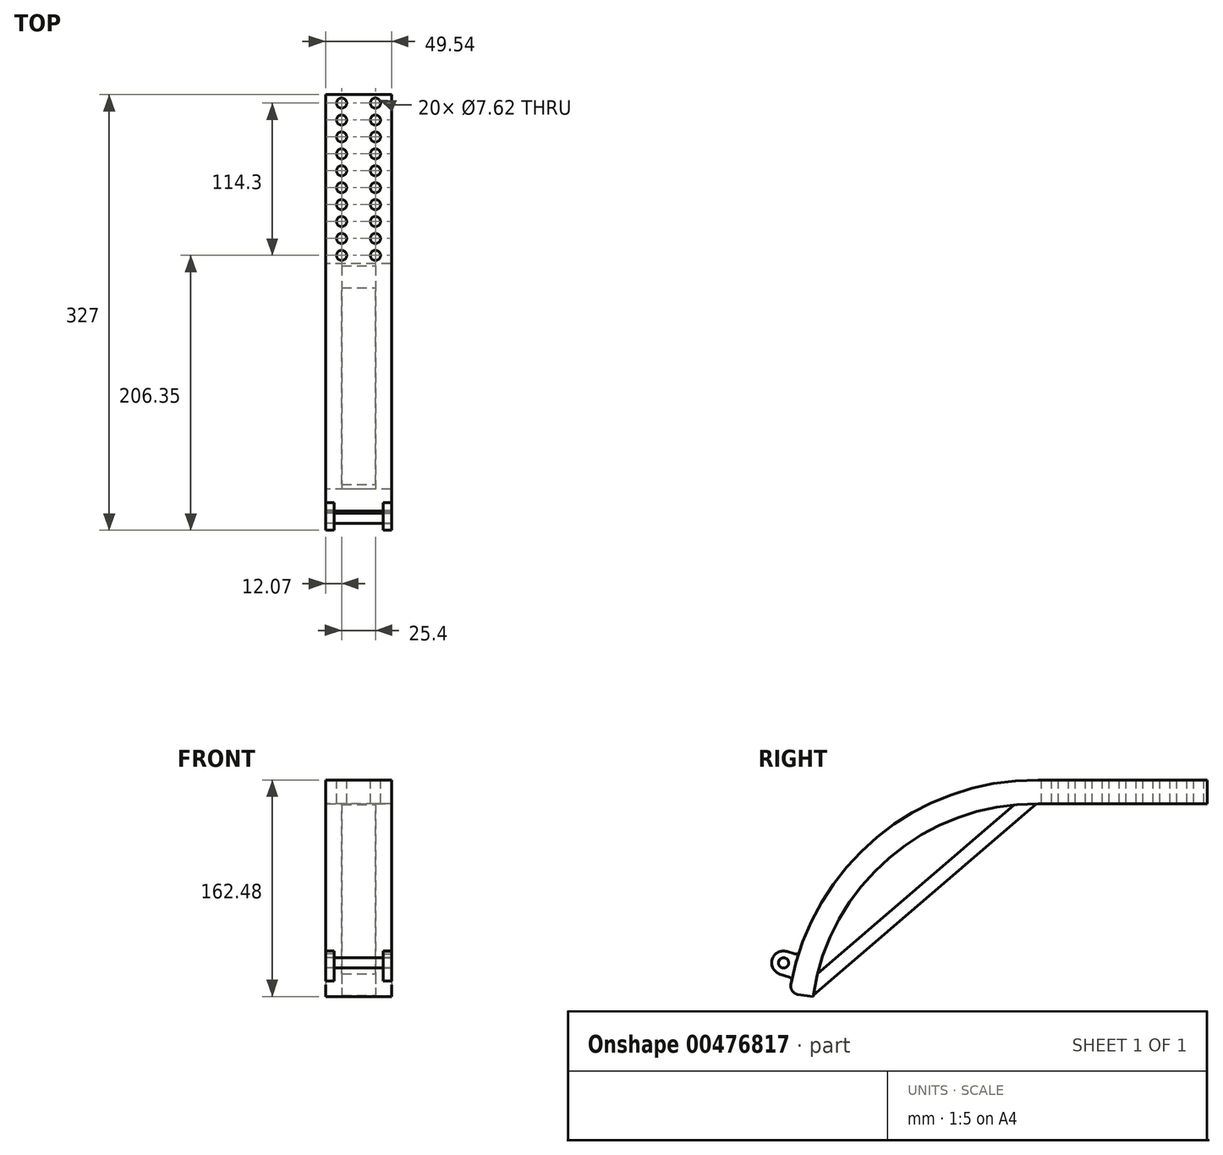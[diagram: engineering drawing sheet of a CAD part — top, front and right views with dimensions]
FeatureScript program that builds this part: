
annotation { "Feature Type Name" : "Feature", "Feature Type Description" : "" }
export const myFeature = defineFeature(function(context is Context, id is Id, definition is map)
    precondition{}
    {
        {
            var Q0;
            Q0=qCreatedBy(makeId("Front.planeOp"),FACE);
            var sketch = newSketch(context, id + "F0", { "sketchPlane" : qUnion([Q0])});
            skLineSegment(sketch, "E0.bottom", {"start": v(24.77, 8.9) * mm, "end": v(-24.77, 8.9) * mm});
            skLineSegment(sketch, "E0.top", {"start": v(24.77, -8.9) * mm, "end": v(-24.77, -8.9) * mm});
            skLineSegment(sketch, "E0.left", {"start": v(24.77, 8.9) * mm, "end": v(24.77, -8.9) * mm});
            skLineSegment(sketch, "E0.right", {"start": v(-24.77, 8.9) * mm, "end": v(-24.77, -8.9) * mm});
            skPoint(sketch, "E0.middle", {"position": v(0, 0) * mm});
            skSolve(sketch);
        }
        {
            var Q0;
            Q0=qCreatedBy(makeId("Right.planeOp"),FACE);
            var sketch = newSketch(context, id + "F1", { "sketchPlane" : qUnion([Q0])});
            skArc(sketch, "E1", {"start": v(0, 0) * mm, "mid": v(-117.53, -42.8) * mm, "end": v(-177.8, -152.4) * mm});
            skSolve(sketch);
        }
        {
            var Q0;
            Q0=makeQuery(id+"F0.imprint","IMPRINT",FACE,{"disambiguationData":[TD([[makeQuery(id+"F0.imprint","IMPRINT",EDGE,{"derivedFrom":sQuery(id+"F0.wireOp",EDGE,"E0.bottom")}),1.0]])]});
            var Q1;
            Q1=sQuery(id+"F1.wireOp",EDGE,"E1");
            sweep(context, id + "F2", {"profiles" : qUnion([Q0]), "path" : qUnion([Q1])});
        }
        {
            var Q0;
            Q0=makeQuery(id+"F0.imprint","IMPRINT",FACE,{"disambiguationData":[TD([[makeQuery(id+"F0.imprint","IMPRINT",EDGE,{"derivedFrom":sQuery(id+"F0.wireOp",EDGE,"E0.bottom")}),1.0]])]});
            extrude(context, id + "F3", {"entities" : qUnion([Q0]), "operationType" : NewBodyOperationType.ADD, "oppositeDirection" : true, "depth" : 127 * mm, "offsetDistance" : 25.4 * mm});
        }
        {
            var Q0;
            Q0=qCreatedBy(makeId("Right.planeOp"),FACE);
            var sketch = newSketch(context, id + "F4", { "sketchPlane" : qUnion([Q0])});
            skLineSegment(sketch, "E2", {"start": v(0, -7.7) * mm, "end": v(-169.13, -153.07) * mm});
            skLineSegment(sketch, "E3", {"start": v(-169.13, -153.07) * mm, "end": v(-175.75, -145.37) * mm});
            skLineSegment(sketch, "E4", {"start": v(-175.75, -145.37) * mm, "end": v(-6.62, 0) * mm});
            skLineSegment(sketch, "E5", {"start": v(-6.62, 0) * mm, "end": v(0, -7.7) * mm});
            skSolve(sketch);
        }
        {
            var Q0;
            Q0=makeQuery(id+"F4.imprint","IMPRINT",FACE,{"disambiguationData":[TD([[makeQuery(id+"F4.imprint","IMPRINT",EDGE,{"derivedFrom":sQuery(id+"F4.wireOp",EDGE,"E2")}),-1.0]])]});
            extrude(context, id + "F5", {"entities" : qUnion([Q0]), "operationType" : NewBodyOperationType.ADD, "depth" : 12.7 * mm, "offsetDistance" : 25.4 * mm, "hasSecondDirection" : true, "secondDirectionOppositeDirection" : true, "secondDirectionDepth" : 12.7 * mm});
        }
        {
            var Q0;
            Q0=qCreatedBy(makeId("Right.planeOp"),FACE);
            var sketch = newSketch(context, id + "F6", { "sketchPlane" : qUnion([Q0])});
            skCircle(sketch, "E6", {"center": v(-191.05, -128.36) * mm, "radius": 3.81 * mm});
            skLineSegment(sketch, "E7", {"start": v(-188.66, -158.5) * mm, "end": v(-188.66, -150.46) * mm, "construction": true});
            skLineSegment(sketch, "E8", {"start": v(-188.66, -150.46) * mm, "end": v(-182.5, -130.81) * mm, "construction": true});
            skLineSegment(sketch, "E9.trimOffspring", {"start": v(-177.02, -113.3) * mm, "end": v(-176.66, -112.17) * mm, "construction": true});
            skPoint(sketch, "E10.start.orphan", {"position": v(-186.61, -151.22) * mm});
            skPoint(sketch, "E11.0.start.orphan", {"position": v(0, 8.9) * mm});
            skSolve(sketch);
        }
        {
            var Q0;
            Q0=makeQuery(id+"F6.imprint","IMPRINT",FACE,{"disambiguationData":[TD([[makeQuery(id+"F6.imprint","IMPRINT",EDGE,{"derivedFrom":sQuery(id+"F6.wireOp",EDGE,"E6")}),1.0]])]});
            var Q1;
            {var subQ0=sQuery(id+"F0.wireOp",EDGE,"E0.left");Q1=makeQuery(id+"F3.boolean.opBoolean","MERGE",FACE,{"derivedFrom":[makeQuery(id+"F2.opSweep","SWEPT_FACE",FACE,{"disambiguationData":[OSD([subQ0,sQuery(id+"F1.wireOp",EDGE,"E1")])]}),makeQuery(id+"F3.opExtrude","SWEPT_FACE",FACE,{"disambiguationData":[OSD([subQ0])]})]});}
            var Q2;
            {var subQ0=sQuery(id+"F0.wireOp",EDGE,"E0.right");Q2=makeQuery(id+"F3.boolean.opBoolean","MERGE",FACE,{"derivedFrom":[makeQuery(id+"F2.opSweep","SWEPT_FACE",FACE,{"disambiguationData":[OSD([subQ0,sQuery(id+"F1.wireOp",EDGE,"E1")])]}),makeQuery(id+"F3.opExtrude","SWEPT_FACE",FACE,{"disambiguationData":[OSD([subQ0])]})]});}
            extrude(context, id + "F7", {"entities" : qUnion([Q0]), "endBound" : BoundingType.UP_TO_SURFACE, "depth" : 50.8 * mm, "endBoundEntityFace" : qUnion([Q1]), "offsetDistance" : 25.4 * mm, "hasSecondDirection" : true, "secondDirectionBound" : SecondDirectionBoundingType.UP_TO_SURFACE, "secondDirectionOppositeDirection" : true, "secondDirectionDepth" : 25.4 * mm, "secondDirectionBoundEntityFace" : qUnion([Q2])});
        }
        {
            var Q0;
            Q0=makeQuery(id+"F2.opSweep","CAP_EDGE",EDGE,{"disambiguationData":[OSD([sQuery(id+"F0.wireOp",EDGE,"E0.bottom"),sQuery(id+"F1.wireOp",VERTEX,"E1.end")])],"isStart":false});
            fillet(context, id + "F8", {"entities" : qUnion([Q0]), "radius" : 6.35 * mm, "tangentPropagation" : true, "allowEdgeOverflow" : false});
        }
        {
            var Q0;
            {var subQ0=sQuery(id+"F0.wireOp",EDGE,"E0.right");Q0=makeQuery(id+"F3.boolean.opBoolean","MERGE",FACE,{"derivedFrom":[makeQuery(id+"F2.opSweep","SWEPT_FACE",FACE,{"disambiguationData":[OSD([subQ0,sQuery(id+"F1.wireOp",EDGE,"E1")])]}),makeQuery(id+"F3.opExtrude","SWEPT_FACE",FACE,{"disambiguationData":[OSD([subQ0])]})]});}
            var sketch = newSketch(context, id + "F9", { "sketchPlane" : qUnion([Q0])});
            skCircle(sketch, "E12.0", {"center": v(191.1, -128.34) * mm, "radius": 3.81 * mm});
            skArc(sketch, "E13", {"start": v(193.88, -136.8) * mm, "mid": v(199.6, -125.7) * mm, "end": v(188.6, -119.81) * mm});
            skLineSegment(sketch, "E14", {"start": v(188.6, -119.81) * mm, "end": v(182.46, -121.61) * mm});
            skLineSegment(sketch, "E15", {"start": v(193.88, -136.8) * mm, "end": v(186.76, -139.13) * mm});
            skPoint(sketch, "E16.orphan", {"position": v(185.55, -144.67) * mm});
            skPoint(sketch, "E17.orphan", {"position": v(0, 8.9) * mm});
            skArc(sketch, "E18.filletArc", {"start": v(186.76, -139.13) * mm, "mid": v(185.36, -140.26) * mm, "end": v(185.05, -142.03) * mm});
            skPoint(sketch, "E19.newPointA", {"position": v(178.86, -122.67) * mm});
            skArc(sketch, "E19.filletArc", {"start": v(179.33, -119.96) * mm, "mid": v(180.56, -121.42) * mm, "end": v(182.46, -121.61) * mm});
            skArc(sketch, "E20.0", {"start": v(179.33, -119.96) * mm, "mid": v(182.53, -130.9) * mm, "end": v(185.05, -142.03) * mm});
            skSolve(sketch);
        }
        {
            var Q0;
            Q0=makeQuery(id+"F9.imprint","IMPRINT",FACE,{"disambiguationData":[TD([[makeQuery(id+"F9.imprint","IMPRINT",EDGE,{"derivedFrom":sQuery(id+"F9.wireOp",EDGE,"E12.0")}),-1.0]])]});
            extrude(context, id + "F10", {"entities" : qUnion([Q0]), "oppositeDirection" : true, "depth" : 6.35 * mm, "offsetDistance" : 25.4 * mm});
        }
        {
            var Q0;
            Q0=makeQuery(id+"F10.opExtrude","SWEPT_BODY",BODY,{"disambiguationData":[OSD([sQuery(id+"F9.wireOp",EDGE,"E12.0"),sQuery(id+"F9.wireOp",EDGE,"E13"),sQuery(id+"F9.wireOp",EDGE,"E14"),sQuery(id+"F9.wireOp",EDGE,"E15"),sQuery(id+"F9.wireOp",EDGE,"E18.filletArc"),sQuery(id+"F9.wireOp",EDGE,"E19.filletArc"),sQuery(id+"F9.wireOp",EDGE,"E20.0")])]});
            var Q1;
            Q1=qCreatedBy(makeId("Right.planeOp"),FACE);
            mirror(context, id + "F11", {"entities" : qUnion([Q0]), "mirrorPlane" : qUnion([Q1])});
        }
        {
            var Q0;
            Q0=makeQuery(id+"F3.opExtrude","SWEPT_FACE",FACE,{"disambiguationData":[OSD([sQuery(id+"F0.wireOp",EDGE,"E0.bottom")])]});
            var sketch = newSketch(context, id + "F12", { "sketchPlane" : qUnion([Q0])});
            skLineSegment(sketch, "E21", {"start": v(0, 127) * mm, "end": v(0, 0) * mm, "construction": true});
            skCircle(sketch, "E22", {"center": v(-12.7, 6.35) * mm, "radius": 3.81 * mm});
            skCircle(sketch, "E23.0.1.0", {"center": v(-12.7, 19.05) * mm, "radius": 3.81 * mm});
            skCircle(sketch, "E23.0.2.0", {"center": v(-12.7, 31.75) * mm, "radius": 3.81 * mm});
            skCircle(sketch, "E23.0.3.0", {"center": v(-12.7, 44.45) * mm, "radius": 3.81 * mm});
            skCircle(sketch, "E23.0.4.0", {"center": v(-12.7, 57.15) * mm, "radius": 3.81 * mm});
            skCircle(sketch, "E23.0.5.0", {"center": v(-12.7, 69.85) * mm, "radius": 3.81 * mm});
            skCircle(sketch, "E23.0.6.0", {"center": v(-12.7, 82.55) * mm, "radius": 3.81 * mm});
            skCircle(sketch, "E23.0.7.0", {"center": v(-12.7, 95.25) * mm, "radius": 3.81 * mm});
            skCircle(sketch, "E23.0.8.0", {"center": v(-12.7, 107.95) * mm, "radius": 3.81 * mm});
            skCircle(sketch, "E23.0.9.0", {"center": v(-12.7, 120.65) * mm, "radius": 3.81 * mm});
            skCircle(sketch, "E23.1.0.0", {"center": v(12.7, 6.35) * mm, "radius": 3.81 * mm});
            skCircle(sketch, "E23.1.1.0", {"center": v(12.7, 19.05) * mm, "radius": 3.81 * mm});
            skCircle(sketch, "E23.1.2.0", {"center": v(12.7, 31.75) * mm, "radius": 3.81 * mm});
            skCircle(sketch, "E23.1.3.0", {"center": v(12.7, 44.45) * mm, "radius": 3.81 * mm});
            skCircle(sketch, "E23.1.4.0", {"center": v(12.7, 57.15) * mm, "radius": 3.81 * mm});
            skCircle(sketch, "E23.1.5.0", {"center": v(12.7, 69.85) * mm, "radius": 3.81 * mm});
            skCircle(sketch, "E23.1.6.0", {"center": v(12.7, 82.55) * mm, "radius": 3.81 * mm});
            skCircle(sketch, "E23.1.7.0", {"center": v(12.7, 95.25) * mm, "radius": 3.81 * mm});
            skCircle(sketch, "E23.1.8.0", {"center": v(12.7, 107.95) * mm, "radius": 3.81 * mm});
            skCircle(sketch, "E23.1.9.0", {"center": v(12.7, 120.65) * mm, "radius": 3.81 * mm});
            skLineSegment(sketch, "E23.direction1", {"start": v(-12.7, 6.35) * mm, "end": v(12.7, 6.35) * mm, "construction": true});
            skLineSegment(sketch, "E23.direction2", {"start": v(-12.7, 6.35) * mm, "end": v(-12.7, 19.05) * mm, "construction": true});
            skSolve(sketch);
        }
        {
            var Q0;
            Q0 = qSketchRegion(id + "F12", true);
            extrude(context, id + "F13", {"entities" : qUnion([Q0]), "operationType" : NewBodyOperationType.REMOVE, "oppositeDirection" : true, "depth" : 25.4 * mm, "offsetDistance" : 25.4 * mm});
        }
    });
